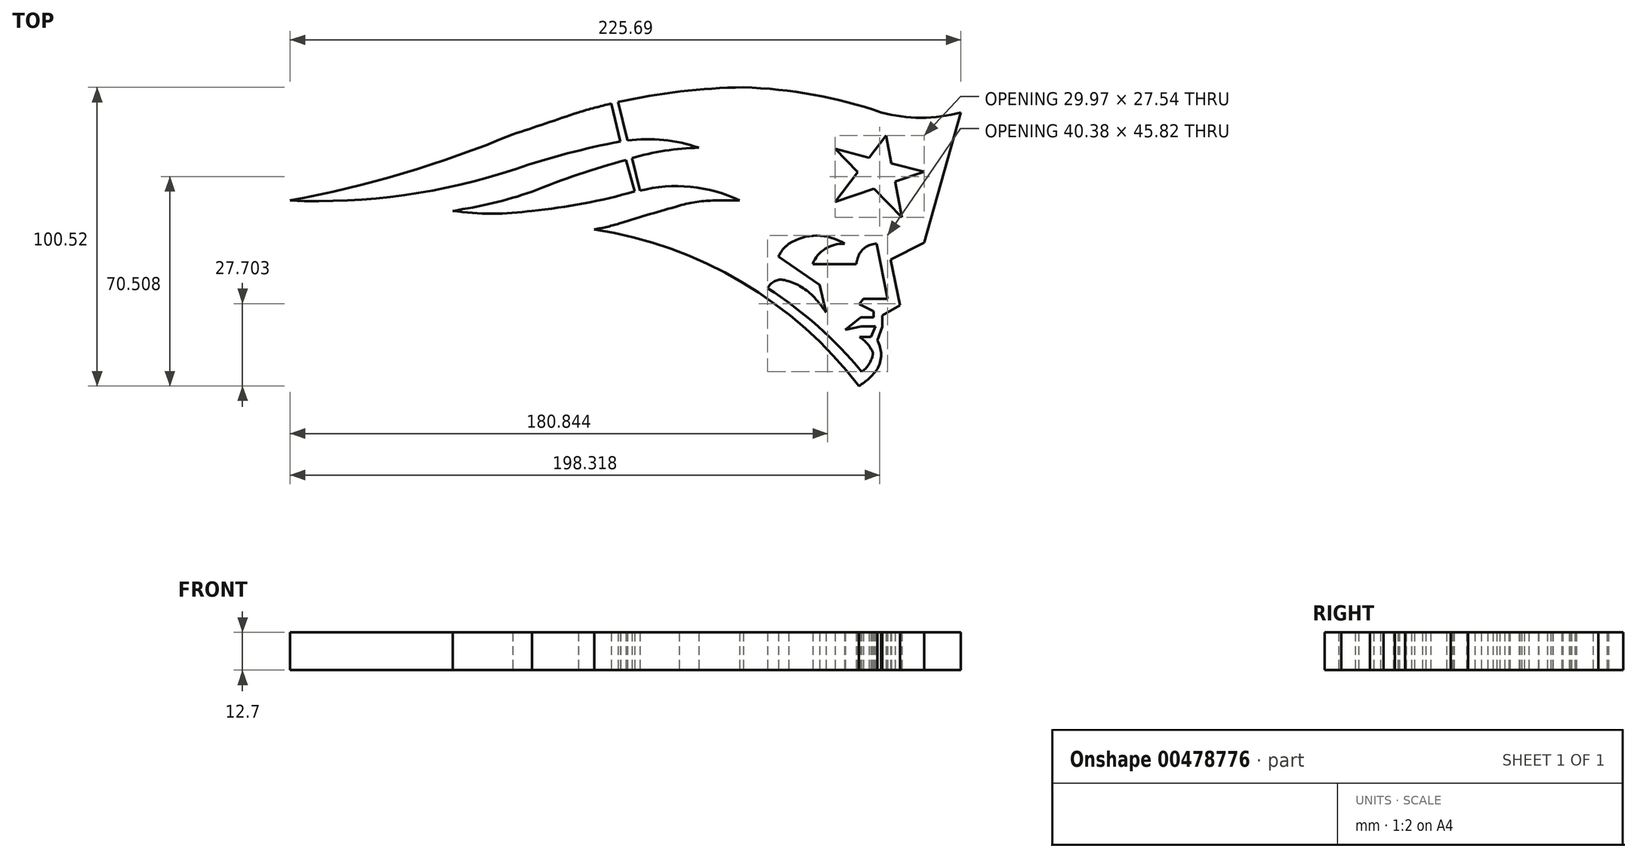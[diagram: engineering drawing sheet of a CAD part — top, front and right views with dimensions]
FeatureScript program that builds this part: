
annotation { "Feature Type Name" : "Feature", "Feature Type Description" : "" }
export const myFeature = defineFeature(function(context is Context, id is Id, definition is map)
    precondition{}
    {
        {
            var Q0;
            Q0=qCreatedBy(makeId("Top.planeOp"),FACE);
            var sketch = newSketch(context, id + "F0", { "sketchPlane" : qUnion([Q0])});
            skPoint(sketch, "E0", {"position": v(109.65, 40.04) * mm});
            skPoint(sketch, "E1", {"position": v(82.81, 40.04) * mm});
            skArc(sketch, "E2", {"start": v(82.81, 40.04) * mm, "mid": v(96.23, 38.23) * mm, "end": v(109.65, 40.04) * mm});
            skPoint(sketch, "E3", {"position": v(-19.1, 40.04) * mm});
            skArc(sketch, "E4", {"start": v(82.81, 40.04) * mm, "mid": v(59.94, 46) * mm, "end": v(36.43, 48.46) * mm});
            skPoint(sketch, "E5", {"position": v(36.43, 48.46) * mm});
            skArc(sketch, "E6", {"start": v(36.43, 48.46) * mm, "mid": v(8.37, 46.16) * mm, "end": v(-19.1, 40.04) * mm});
            skLineSegment(sketch, "E7", {"start": v(-5.67, 43.53) * mm, "end": v(-2.51, 30.59) * mm});
            skLineSegment(sketch, "E8", {"start": v(-8.02, 42.99) * mm, "end": v(-4.91, 30.25) * mm});
            skArc(sketch, "E9", {"start": v(21.43, 28.16) * mm, "mid": v(9.6, 30.73) * mm, "end": v(-2.51, 30.59) * mm});
            skLineSegment(sketch, "E10", {"start": v(-2.51, 30.59) * mm, "end": v(1.62, 13.65) * mm});
            skLineSegment(sketch, "E11", {"start": v(-3.05, 24.03) * mm, "end": v(-0.18, 13.42) * mm});
            skArc(sketch, "E12", {"start": v(21.43, 28.16) * mm, "mid": v(10.07, 27.12) * mm, "end": v(-1.07, 24.66) * mm});
            skArc(sketch, "E13", {"start": v(35.16, 10.36) * mm, "mid": v(18.68, 14.97) * mm, "end": v(1.62, 13.65) * mm});
            skLineSegment(sketch, "E14", {"start": v(35.16, 10.36) * mm, "end": v(26.9, 10.36) * mm});
            skArc(sketch, "E15", {"start": v(26.9, 10.36) * mm, "mid": v(20.84, 9.93) * mm, "end": v(14.9, 8.62) * mm});
            skArc(sketch, "E16", {"start": v(14.9, 8.62) * mm, "mid": v(5.04, 5.78) * mm, "end": v(-4.78, 2.81) * mm});
            skArc(sketch, "E17", {"start": v(-13.7, 0.65) * mm, "mid": v(-9.2, 1.56) * mm, "end": v(-4.78, 2.81) * mm});
            skArc(sketch, "E18", {"start": v(75.36, -52.06) * mm, "mid": v(35.9, -17.12) * mm, "end": v(-13.7, 0.65) * mm});
            skLineSegment(sketch, "E19", {"start": v(109.65, 40.04) * mm, "end": v(97.26, -3.8) * mm});
            skLineSegment(sketch, "E20", {"start": v(97.26, -3.8) * mm, "end": v(85.97, -9.6) * mm});
            skLineSegment(sketch, "E21", {"start": v(85.97, -9.6) * mm, "end": v(89.13, -24.91) * mm});
            skLineSegment(sketch, "E22", {"start": v(89.13, -24.91) * mm, "end": v(83.2, -28.37) * mm});
            skLineSegment(sketch, "E23", {"start": v(83.2, -28.37) * mm, "end": v(83.2, -32.16) * mm});
            skLineSegment(sketch, "E24", {"start": v(83.2, -32.16) * mm, "end": v(81.48, -36.7) * mm});
            skArc(sketch, "E25", {"start": v(81.48, -46.41) * mm, "mid": v(82.76, -41.56) * mm, "end": v(81.48, -36.7) * mm});
            skArc(sketch, "E26", {"start": v(75.36, -52.06) * mm, "mid": v(78.7, -49.54) * mm, "end": v(81.48, -46.41) * mm});
            skArc(sketch, "E27", {"start": v(-3.05, 24.03) * mm, "mid": v(-19.03, 19.16) * mm, "end": v(-34.7, 13.34) * mm});
            skArc(sketch, "E28", {"start": v(-61.39, 6.91) * mm, "mid": v(-47.88, 9.47) * mm, "end": v(-34.7, 13.34) * mm});
            skArc(sketch, "E29", {"start": v(-61.39, 6.91) * mm, "mid": v(-48.04, 5.93) * mm, "end": v(-34.7, 6.91) * mm});
            skArc(sketch, "E30", {"start": v(-34.7, 6.91) * mm, "mid": v(-17.28, 9.36) * mm, "end": v(-0.18, 13.42) * mm});
            skArc(sketch, "E31", {"start": v(-41.15, 32.65) * mm, "mid": v(-30.11, 36.3) * mm, "end": v(-19.1, 40.04) * mm});
            skArc(sketch, "E32", {"start": v(-116.04, 10.36) * mm, "mid": v(-77.5, 19.67) * mm, "end": v(-40.16, 33.06) * mm});
            skArc(sketch, "E33", {"start": v(-4.91, 30.25) * mm, "mid": v(-22.7, 26.24) * mm, "end": v(-40.16, 20.99) * mm});
            skArc(sketch, "E34", {"start": v(-116.04, 10.36) * mm, "mid": v(-77.62, 12.2) * mm, "end": v(-40.16, 20.99) * mm});
            skLineSegment(sketch, "E35", {"start": v(84.47, 32.22) * mm, "end": v(86.28, 22.87) * mm});
            skLineSegment(sketch, "E36", {"start": v(89.8, 4.68) * mm, "end": v(80.4, 14.33) * mm});
            skLineSegment(sketch, "E37", {"start": v(67.3, 27.8) * mm, "end": v(78.77, 24.82) * mm});
            skLineSegment(sketch, "E38", {"start": v(97.26, 20.02) * mm, "end": v(87.47, 16.72) * mm});
            skLineSegment(sketch, "E39", {"start": v(67.3, 9.91) * mm, "end": v(74.98, 19.9) * mm});
            skLineSegment(sketch, "E40.trimOffspring", {"start": v(87.47, 16.72) * mm, "end": v(89.8, 4.68) * mm});
            skLineSegment(sketch, "E41.trimOffspring", {"start": v(86.28, 22.87) * mm, "end": v(97.26, 20.02) * mm});
            skLineSegment(sketch, "E42.trimOffspring", {"start": v(78.77, 24.82) * mm, "end": v(84.47, 32.22) * mm});
            skLineSegment(sketch, "E43.trimOffspring", {"start": v(74.98, 19.9) * mm, "end": v(67.3, 27.8) * mm});
            skLineSegment(sketch, "E44.trimOffspring", {"start": v(80.4, 14.33) * mm, "end": v(67.3, 9.91) * mm});
            skArc(sketch, "E45", {"start": v(76.22, -47.27) * mm, "mid": v(61.53, -31.98) * mm, "end": v(44.62, -19.18) * mm});
            skArc(sketch, "E46", {"start": v(76.22, -47.27) * mm, "mid": v(78.61, -44.86) * mm, "end": v(79.92, -41.73) * mm});
            skArc(sketch, "E47", {"start": v(79.92, -40.56) * mm, "mid": v(78.04, -37.77) * mm, "end": v(75.52, -35.52) * mm});
            skArc(sketch, "E48", {"start": v(79.92, -41.73) * mm, "mid": v(80, -41.15) * mm, "end": v(79.92, -40.56) * mm});
            skLineSegment(sketch, "E49", {"start": v(75.52, -35.52) * mm, "end": v(79.42, -35.52) * mm});
            skLineSegment(sketch, "E50", {"start": v(79.42, -35.52) * mm, "end": v(80.91, -32.02) * mm});
            skLineSegment(sketch, "E51", {"start": v(80.91, -32.02) * mm, "end": v(76.15, -32.02) * mm});
            skLineSegment(sketch, "E52", {"start": v(76.15, -32.02) * mm, "end": v(70.67, -33.17) * mm});
            skLineSegment(sketch, "E53", {"start": v(70.67, -33.17) * mm, "end": v(75.92, -28.92) * mm});
            skLineSegment(sketch, "E54", {"start": v(75.92, -28.92) * mm, "end": v(80.25, -28.92) * mm});
            skLineSegment(sketch, "E55", {"start": v(80.25, -28.92) * mm, "end": v(80.25, -26.92) * mm});
            skLineSegment(sketch, "E56", {"start": v(80.25, -26.92) * mm, "end": v(75.37, -24.52) * mm});
            skLineSegment(sketch, "E57", {"start": v(75.37, -24.52) * mm, "end": v(76.77, -22.77) * mm});
            skLineSegment(sketch, "E58", {"start": v(76.77, -22.77) * mm, "end": v(85, -22.77) * mm});
            skLineSegment(sketch, "E59", {"start": v(85, -22.77) * mm, "end": v(81.27, -4.22) * mm});
            skArc(sketch, "E60", {"start": v(81.27, -4.22) * mm, "mid": v(77.32, -5.48) * mm, "end": v(74.97, -8.89) * mm});
            skArc(sketch, "E61", {"start": v(74.97, -8.89) * mm, "mid": v(74.67, -9.95) * mm, "end": v(74.4, -11.03) * mm});
            skLineSegment(sketch, "E62", {"start": v(74.4, -11.03) * mm, "end": v(59.76, -11.03) * mm});
            skArc(sketch, "E63", {"start": v(70.51, -4.26) * mm, "mid": v(64.01, -5.85) * mm, "end": v(59.76, -11.03) * mm});
            skPoint(sketch, "E64", {"position": v(51.7, -4.26) * mm});
            skArc(sketch, "E65", {"start": v(70.51, -4.26) * mm, "mid": v(61.1, -1.45) * mm, "end": v(51.7, -4.26) * mm});
            skArc(sketch, "E66", {"start": v(51.7, -4.26) * mm, "mid": v(49.7, -6.14) * mm, "end": v(48.3, -8.48) * mm});
            skLineSegment(sketch, "E67", {"start": v(48.3, -8.48) * mm, "end": v(62.08, -18.03) * mm});
            skLineSegment(sketch, "E68", {"start": v(62.08, -18.03) * mm, "end": v(64.28, -27.3) * mm});
            skArc(sketch, "E69", {"start": v(64.28, -27.3) * mm, "mid": v(62.15, -24.44) * mm, "end": v(59.83, -21.72) * mm});
            skArc(sketch, "E70", {"start": v(59.83, -21.72) * mm, "mid": v(55.42, -18.41) * mm, "end": v(50.27, -16.42) * mm});
            skArc(sketch, "E71", {"start": v(50.27, -16.42) * mm, "mid": v(46.95, -16.8) * mm, "end": v(44.62, -19.18) * mm});
            skSolve(sketch);
        }
        {
            var Q0;
            {var subQ3=sQuery(id+"F0.wireOp",EDGE,"E8");Q0=makeQuery(id+"F0.imprint","IMPRINT",FACE,{"disambiguationData":[TD([[makeQuery(id+"F0.imprint","IMPRINT",EDGE,{"derivedFrom":subQ3}),-1.0]])]});}
            var Q1;
            Q1=makeQuery(id+"F0.imprint","IMPRINT",FACE,{"disambiguationData":[TD([[makeQuery(id+"F0.imprint","IMPRINT",EDGE,{"derivedFrom":sQuery(id+"F0.wireOp",EDGE,"E2")}),-1.0]])]});
            var Q2;
            Q2=makeQuery(id+"F0.imprint","IMPRINT",FACE,{"disambiguationData":[TD([[makeQuery(id+"F0.imprint","IMPRINT",EDGE,{"derivedFrom":sQuery(id+"F0.wireOp",EDGE,"E11")}),-1.0]])]});
            extrude(context, id + "F1", {"entities" : qUnion([Q0, Q1, Q2]), "depth" : 12.7 * mm});
        }
    });
